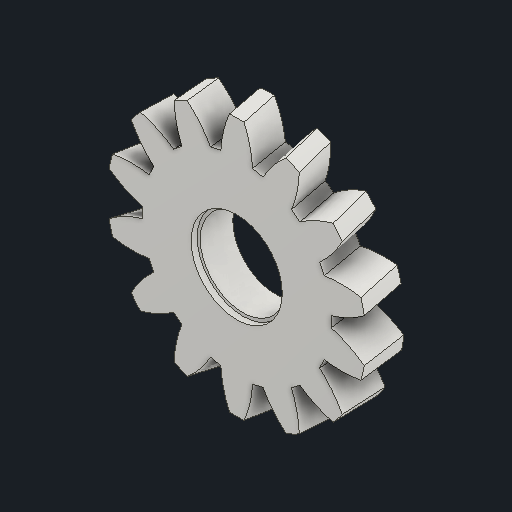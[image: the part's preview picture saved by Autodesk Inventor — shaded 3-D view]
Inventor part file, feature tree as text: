
AUTODESK INVENTOR PART (.ipt)
format: ipt  version: 2024.2 (Build 282272000, 272)  size: 367,104 bytes
history: native  units: in
note: dims shown in document units (in); Inventor stores cm internally (conversion verified against a paired STEP export)
features: other x12, plane x3, sketch x2
ambient origin geometry x8: Origin, YZ Plane, XZ Plane, XY Plane, X Axis, Y Axis, Z Axis, Center Point
bodies: Solid1 (feature_tree)
feature tree (17):
  other  "Spur Gear2"
  other  "Solid1::Spur Gear2"
  other  "TaggingFeature1"
  sketch  "Sketch1"  dims[d0=0.3937in]
  sketch  "Sketch2"  dims[d9=0.0in d14=0.0in d15=1.3982in d16=0.0in d17=0.0in d18=0.0in d19=1.3982in]
  plane  "XZ Plane_1"
  plane  "Work Plane2"
  plane  "Work Plane3"
  other  "Srf1"
  other  "Srf1::Derived"
  other  "Start plane iMate"
  other  "Distance iMate"
  other  "Position iMate"
  other  "Mesh iMate"
  other  "Axis iMate"
  other  "Mesh iMate2"
  other  "Align iMate"
